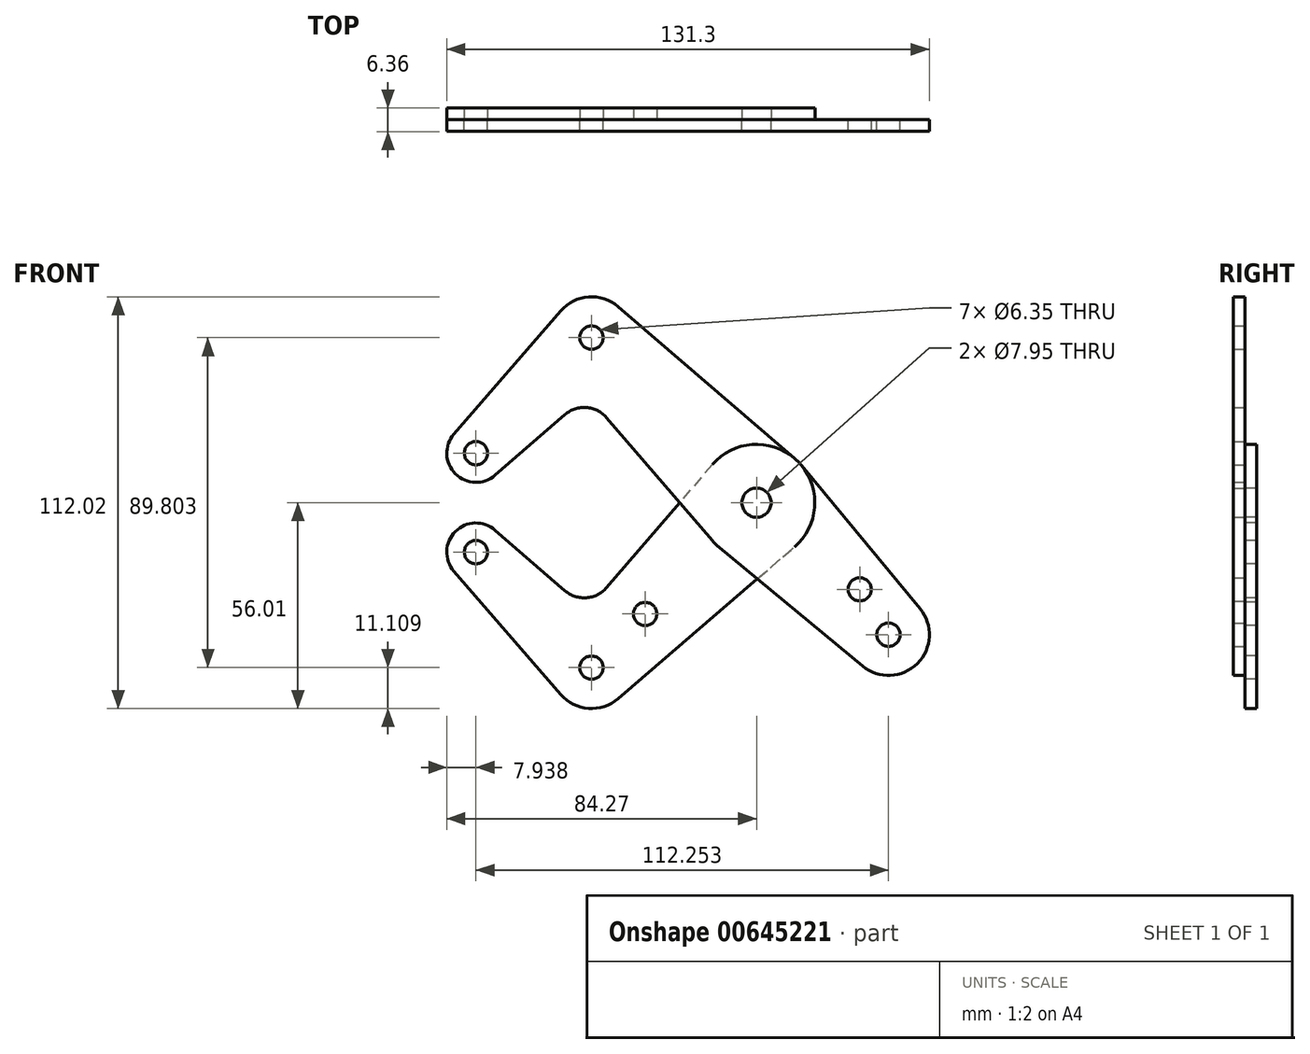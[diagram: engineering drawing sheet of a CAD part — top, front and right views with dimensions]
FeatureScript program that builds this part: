
annotation { "Feature Type Name" : "Feature", "Feature Type Description" : "" }
export const myFeature = defineFeature(function(context is Context, id is Id, definition is map)
    precondition{}
    {
        {
            var Q0;
            Q0=qCreatedBy(makeId("Front.planeOp"),FACE);
            var sketch = newSketch(context, id + "F0", { "sketchPlane" : qUnion([Q0])});
            skCircle(sketch, "E0", {"center": v(0, 0) * mm, "radius": 15.88 * mm});
            skCircle(sketch, "E1", {"center": v(-44.9, 44.9) * mm, "radius": 11.11 * mm});
            skCircle(sketch, "E2", {"center": v(35.92, -35.92) * mm, "radius": 11.11 * mm});
            skLineSegment(sketch, "E3", {"start": v(-44.9, 44.9) * mm, "end": v(81.3, -81.3) * mm, "construction": true});
            skLineSegment(sketch, "E4", {"start": v(-44.9, 44.9) * mm, "end": v(-76.33, 13.47) * mm, "construction": true});
            skCircle(sketch, "E5", {"center": v(-76.33, 13.47) * mm, "radius": 7.94 * mm});
            skCircle(sketch, "E6", {"center": v(-76.33, 13.47) * mm, "radius": 3.18 * mm});
            skCircle(sketch, "E7", {"center": v(0, 0) * mm, "radius": 3.17 * mm});
            skCircle(sketch, "E8", {"center": v(35.92, -35.92) * mm, "radius": 3.18 * mm});
            skCircle(sketch, "E9", {"center": v(28.07, -23.58) * mm, "radius": 3.17 * mm});
            skLineSegment(sketch, "E10", {"start": v(28.07, -23.58) * mm, "end": v(41.22, -10.43) * mm, "construction": true});
            skLineSegment(sketch, "E11", {"start": v(0, 0) * mm, "end": v(20.17, 20.17) * mm, "construction": true});
            skLineSegment(sketch, "E12", {"start": v(28.07, -23.58) * mm, "end": v(48.24, -43.75) * mm, "construction": true});
            skCircle(sketch, "E13", {"center": v(0, 0) * mm, "radius": 3.98 * mm});
            skLineSegment(sketch, "E14", {"start": v(-76.33, 13.47) * mm, "end": v(-76.33, -13.47) * mm, "construction": true});
            skLineSegment(sketch, "E15", {"start": v(0, 0) * mm, "end": v(-44.9, -44.9) * mm, "construction": true});
            skLineSegment(sketch, "E16", {"start": v(-44.9, -44.9) * mm, "end": v(-76.33, -13.47) * mm, "construction": true});
            skCircle(sketch, "E17", {"center": v(-76.33, -13.47) * mm, "radius": 7.94 * mm});
            skCircle(sketch, "E18", {"center": v(-44.9, -44.9) * mm, "radius": 11.11 * mm});
            skCircle(sketch, "E19", {"center": v(-30.3, -30.3) * mm, "radius": 3.18 * mm});
            skLineSegment(sketch, "E20", {"start": v(-53.3, 52.18) * mm, "end": v(-82.33, 18.67) * mm});
            skLineSegment(sketch, "E21", {"start": v(-82.33, -18.67) * mm, "end": v(-53.3, -52.18) * mm});
            skCircle(sketch, "E22", {"center": v(-44.9, 44.9) * mm, "radius": 3.18 * mm});
            skLineSegment(sketch, "E23", {"start": v(-37.66, -53.33) * mm, "end": v(10.35, -12.04) * mm});
            skLineSegment(sketch, "E24", {"start": v(-71.13, -7.47) * mm, "end": v(-52.08, -23.98) * mm});
            skLineSegment(sketch, "E25", {"start": v(-12.04, 10.35) * mm, "end": v(-40.85, -23.15) * mm});
            skLineSegment(sketch, "E26", {"start": v(-10.12, -12.23) * mm, "end": v(28.83, -44.48) * mm});
            skLineSegment(sketch, "E27", {"start": v(-71.13, 7.47) * mm, "end": v(-52.08, 23.98) * mm});
            skLineSegment(sketch, "E28", {"start": v(-40.85, 23.15) * mm, "end": v(-12.04, -10.35) * mm});
            skLineSegment(sketch, "E29", {"start": v(-37.66, 53.33) * mm, "end": v(10.35, 12.04) * mm});
            skLineSegment(sketch, "E30", {"start": v(12.23, 10.12) * mm, "end": v(44.48, -28.83) * mm});
            skLineSegment(sketch, "E31", {"start": v(28.07, -23.58) * mm, "end": v(25.83, -25.83) * mm});
            skArc(sketch, "E32.filletArc", {"start": v(-52.08, -23.98) * mm, "mid": v(-46.3, -25.9) * mm, "end": v(-40.85, -23.15) * mm});
            skArc(sketch, "E33.filletArc", {"start": v(-40.85, 23.15) * mm, "mid": v(-46.3, 25.9) * mm, "end": v(-52.08, 23.98) * mm});
            skCircle(sketch, "E34", {"center": v(-76.33, -13.47) * mm, "radius": 3.18 * mm});
            skCircle(sketch, "E35", {"center": v(-44.9, -44.9) * mm, "radius": 3.18 * mm});
            skSolve(sketch);
        }
        {
            var Q0;
            {var subQ0=sQuery(id+"F0.wireOp",EDGE,"E20");Q0=makeQuery(id+"F0.imprint","IMPRINT",FACE,{"disambiguationData":[TD([[makeQuery(id+"F0.imprint","IMPRINT",EDGE,{"derivedFrom":subQ0}),1.0]])]});}
            var Q1;
            Q1=makeQuery(id+"F0.imprint","IMPRINT",FACE,{"disambiguationData":[TD([[makeQuery(id+"F0.imprint","IMPRINT",EDGE,{"derivedFrom":sQuery(id+"F0.wireOp",EDGE,"E9")}),-1.0]])]});
            var Q2;
            {var subQ0=sQuery(id+"F0.wireOp",EDGE,"E25");var subQ1=sQuery(id+"F0.wireOp",EDGE,"E0");var subQ2=makeQuery(id+"F0.imprint","INTERSECT",VERTEX,{"derivedFrom":[subQ1,subQ0]});Q2=makeQuery(id+"F0.imprint","IMPRINT",FACE,{"disambiguationData":[TD([[makeQuery(id+"F0.imprint","IMPRINT",EDGE,{"disambiguationData":[TD([[subQ2,-1.0]])],"derivedFrom":subQ1}),-1.0]])]});}
            var Q3;
            {var subQ0=sQuery(id+"F0.wireOp",EDGE,"E23");var subQ1=sQuery(id+"F0.wireOp",EDGE,"E0");var subQ2=makeQuery(id+"F0.imprint","INTERSECT",VERTEX,{"derivedFrom":[subQ1,subQ0]});Q3=makeQuery(id+"F0.imprint","IMPRINT",FACE,{"disambiguationData":[TD([[makeQuery(id+"F0.imprint","IMPRINT",EDGE,{"disambiguationData":[TD([[subQ2,1.0]])],"derivedFrom":subQ1}),-1.0]])]});}
            var Q4;
            Q4=makeQuery(id+"F0.imprint","IMPRINT",FACE,{"disambiguationData":[TD([[makeQuery(id+"F0.imprint","IMPRINT",EDGE,{"derivedFrom":sQuery(id+"F0.wireOp",EDGE,"E22")}),-1.0]])]});
            var Q5;
            Q5=makeQuery(id+"F0.imprint","IMPRINT",FACE,{"disambiguationData":[TD([[makeQuery(id+"F0.imprint","IMPRINT",EDGE,{"derivedFrom":sQuery(id+"F0.wireOp",EDGE,"E6")}),-1.0]])]});
            var Q6;
            Q6=makeQuery(id+"F0.imprint","IMPRINT",FACE,{"disambiguationData":[TD([[makeQuery(id+"F0.imprint","IMPRINT",EDGE,{"derivedFrom":sQuery(id+"F0.wireOp",EDGE,"E13")}),-1.0]])]});
            var Q7;
            Q7=makeQuery(id+"F0.imprint","IMPRINT",FACE,{"disambiguationData":[TD([[makeQuery(id+"F0.imprint","IMPRINT",EDGE,{"derivedFrom":sQuery(id+"F0.wireOp",EDGE,"E8")}),-1.0]])]});
            extrude(context, id + "F1", {"entities" : qUnion([Q0, Q1, Q2, Q3, Q4, Q5, Q6, Q7]), "depth" : 3.17 * mm, "offsetDistance" : 25.4 * mm});
        }
        {
            var Q0;
            Q0=makeQuery(id+"F0.imprint","IMPRINT",FACE,{"disambiguationData":[TD([[makeQuery(id+"F0.imprint","IMPRINT",EDGE,{"derivedFrom":sQuery(id+"F0.wireOp",EDGE,"E19")}),-1.0]])]});
            var Q1;
            Q1=makeQuery(id+"F0.imprint","IMPRINT",FACE,{"disambiguationData":[TD([[makeQuery(id+"F0.imprint","IMPRINT",EDGE,{"derivedFrom":sQuery(id+"F0.wireOp",EDGE,"E35")}),-1.0]])]});
            var Q2;
            Q2=makeQuery(id+"F0.imprint","IMPRINT",FACE,{"disambiguationData":[TD([[makeQuery(id+"F0.imprint","IMPRINT",EDGE,{"derivedFrom":sQuery(id+"F0.wireOp",EDGE,"E34")}),-1.0]])]});
            var Q3;
            Q3=makeQuery(id+"F0.imprint","IMPRINT",FACE,{"disambiguationData":[TD([[makeQuery(id+"F0.imprint","IMPRINT",EDGE,{"derivedFrom":sQuery(id+"F0.wireOp",EDGE,"E13")}),-1.0]])]});
            var Q4;
            {var subQ0=sQuery(id+"F0.wireOp",EDGE,"E25");var subQ1=sQuery(id+"F0.wireOp",EDGE,"E0");var subQ2=makeQuery(id+"F0.imprint","INTERSECT",VERTEX,{"derivedFrom":[subQ1,subQ0]});Q4=makeQuery(id+"F0.imprint","IMPRINT",FACE,{"disambiguationData":[TD([[makeQuery(id+"F0.imprint","IMPRINT",EDGE,{"disambiguationData":[TD([[subQ2,-1.0]])],"derivedFrom":subQ1}),-1.0]])]});}
            var Q5;
            {var subQ0=sQuery(id+"F0.wireOp",EDGE,"E23");var subQ1=sQuery(id+"F0.wireOp",EDGE,"E0");var subQ2=makeQuery(id+"F0.imprint","INTERSECT",VERTEX,{"derivedFrom":[subQ1,subQ0]});Q5=makeQuery(id+"F0.imprint","IMPRINT",FACE,{"disambiguationData":[TD([[makeQuery(id+"F0.imprint","IMPRINT",EDGE,{"disambiguationData":[TD([[subQ2,1.0]])],"derivedFrom":subQ1}),-1.0]])]});}
            extrude(context, id + "F2", {"entities" : qUnion([Q0, Q1, Q2, Q3, Q4, Q5]), "oppositeDirection" : true, "depth" : 3.17 * mm, "offsetDistance" : 25.4 * mm});
        }
    });
